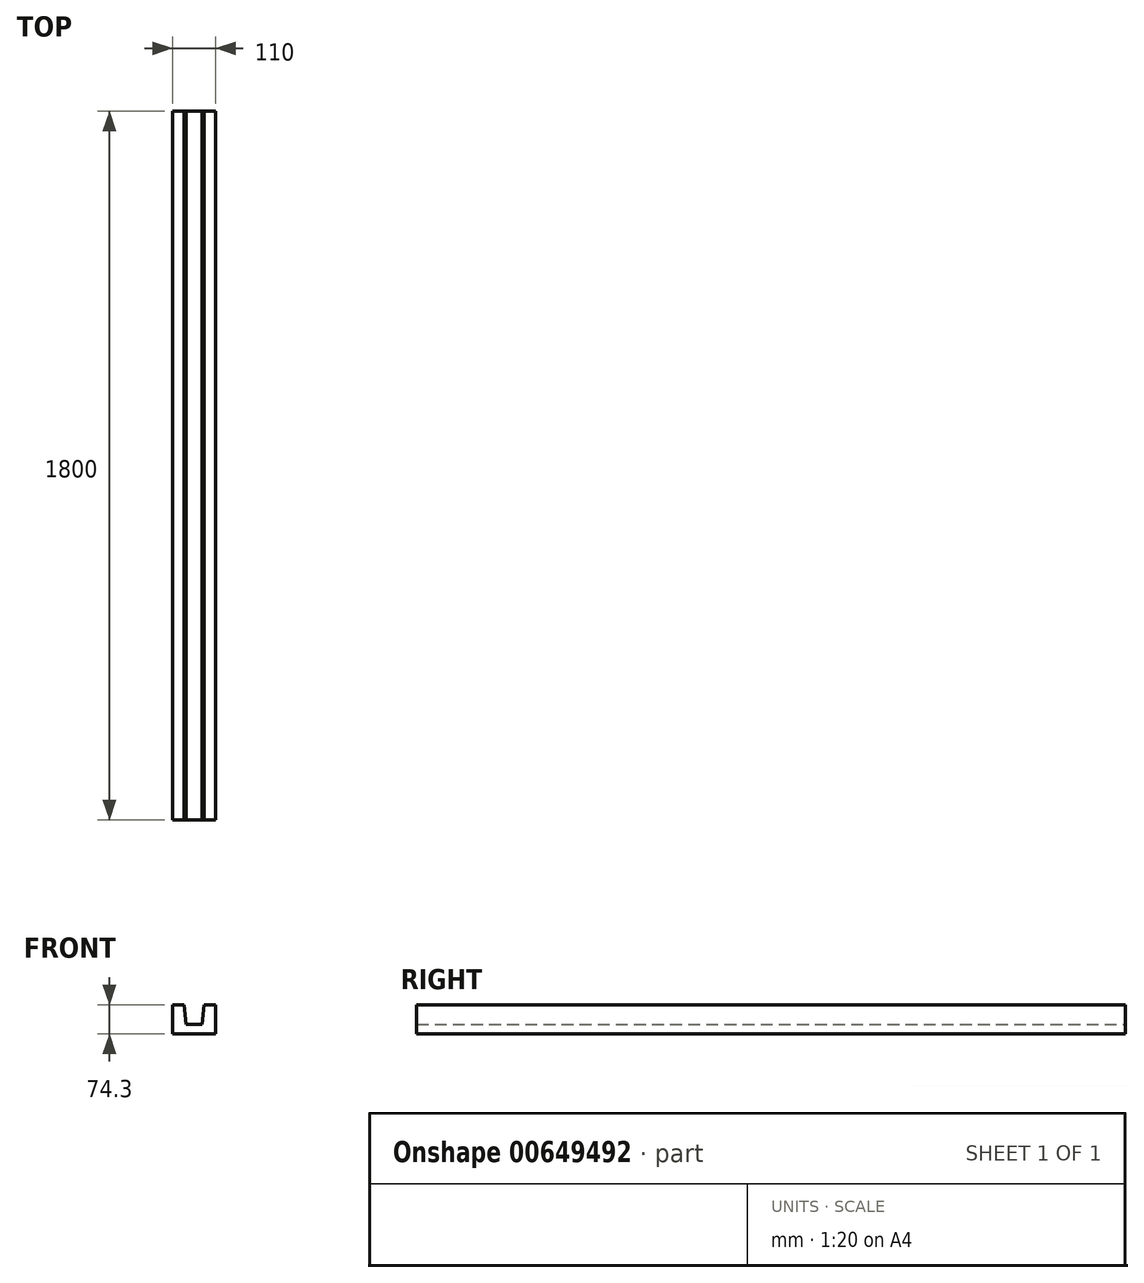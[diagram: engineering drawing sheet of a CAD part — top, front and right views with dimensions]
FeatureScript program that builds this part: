
annotation { "Feature Type Name" : "Feature", "Feature Type Description" : "" }
export const myFeature = defineFeature(function(context is Context, id is Id, definition is map)
    precondition{}
    {
        {
            var Q0;
            Q0=qCreatedBy(makeId("Front.planeOp"),FACE);
            var sketch = newSketch(context, id + "F0", { "sketchPlane" : qUnion([Q0])});
            skLineSegment(sketch, "E0", {"start": v(0, 0) * mm, "end": v(20, 0) * mm});
            skLineSegment(sketch, "E1", {"start": v(20, 0) * mm, "end": v(25, 50) * mm});
            skLineSegment(sketch, "E2", {"start": v(25, 50) * mm, "end": v(55, 50) * mm});
            skLineSegment(sketch, "E3", {"start": v(55, 50) * mm, "end": v(55, -24.3) * mm});
            skLineSegment(sketch, "E4", {"start": v(55, -24.3) * mm, "end": v(0, -24.3) * mm});
            skLineSegment(sketch, "E5", {"start": v(20, 0) * mm, "end": v(20, 75.33) * mm, "construction": true});
            skLineSegment(sketch, "E6.MirrorCS", {"start": v(-55, 50) * mm, "end": v(-55, -24.3) * mm});
            skLineSegment(sketch, "E7.MirrorCS", {"start": v(-25, 50) * mm, "end": v(-55, 50) * mm});
            skLineSegment(sketch, "E8.MirrorCS", {"start": v(-20, 0) * mm, "end": v(-25, 50) * mm});
            skLineSegment(sketch, "E9.MirrorCS", {"start": v(-55, -24.3) * mm, "end": v(0, -24.3) * mm});
            skLineSegment(sketch, "E10.MirrorCS", {"start": v(0, 0) * mm, "end": v(-20, 0) * mm});
            skSolve(sketch);
        }
        {
            var Q0;
            Q0 = qSketchRegion(id + "F0", true);
            extrude(context, id + "F1", {"entities" : qUnion([Q0]), "depth" : 1800 * mm, "offsetDistance" : 25 * mm});
        }
    });
